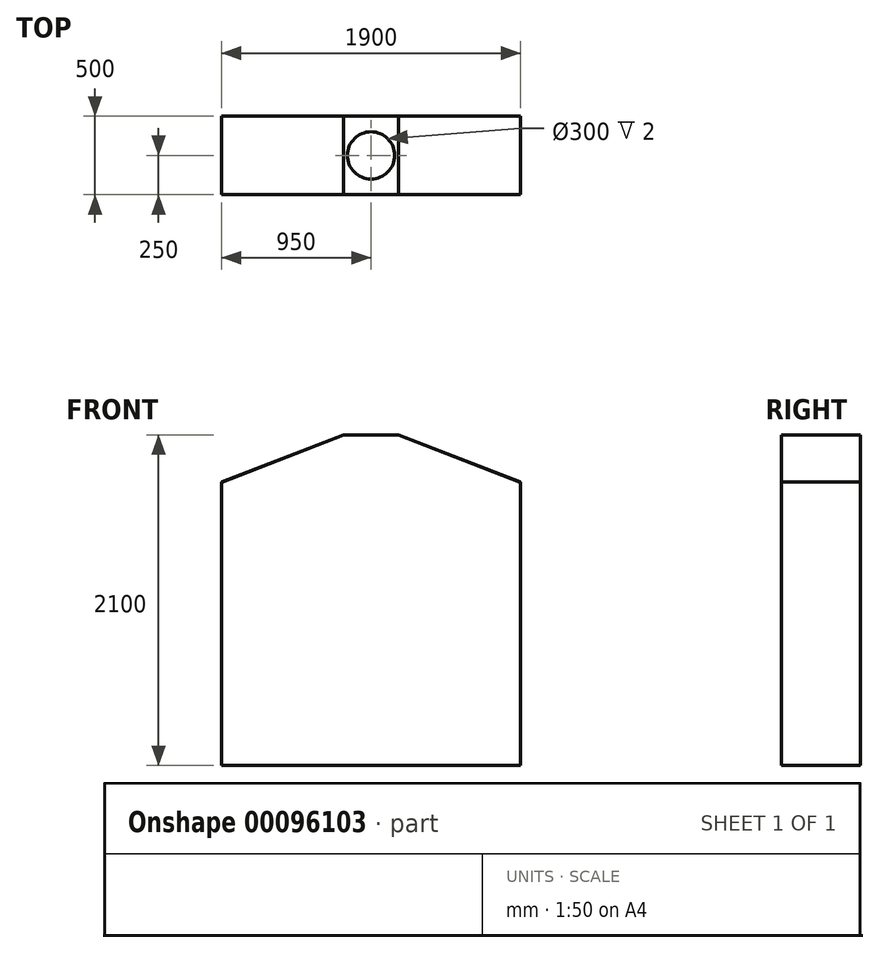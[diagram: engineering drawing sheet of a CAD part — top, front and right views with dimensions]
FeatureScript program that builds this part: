
annotation { "Feature Type Name" : "Feature", "Feature Type Description" : "" }
export const myFeature = defineFeature(function(context is Context, id is Id, definition is map)
    precondition{}
    {
        {
            var Q0;
            Q0=qCreatedBy(makeId("Front.planeOp"),FACE);
            var sketch = newSketch(context, id + "F0", { "sketchPlane" : qUnion([Q0])});
            skLineSegment(sketch, "E0.bottom", {"start": v(950, -900) * mm, "end": v(-950, -900) * mm});
            skLineSegment(sketch, "E0.top", {"start": v(950, 900) * mm, "end": v(-950, 900) * mm});
            skLineSegment(sketch, "E0.left", {"start": v(950, -900) * mm, "end": v(950, 900) * mm});
            skLineSegment(sketch, "E0.right", {"start": v(-950, -900) * mm, "end": v(-950, 900) * mm});
            skPoint(sketch, "E0.middle", {"position": v(0, 0) * mm});
            skLineSegment(sketch, "E1", {"start": v(0, 1200) * mm, "end": v(-175, 1200) * mm});
            skLineSegment(sketch, "E2", {"start": v(0, 1200) * mm, "end": v(175, 1200) * mm});
            skLineSegment(sketch, "E3", {"start": v(-950, 900) * mm, "end": v(-175, 1200) * mm});
            skLineSegment(sketch, "E4", {"start": v(175, 1200) * mm, "end": v(950, 900) * mm});
            skSolve(sketch);
        }
        {
            var Q0;
            Q0 = qSketchRegion(id + "F0", true);
            extrude(context, id + "F1", {"entities" : qUnion([Q0]), "endBound" : BoundingType.SYMMETRIC, "depth" : 500 * mm});
        }
        {
            var Q0;
            Q0=makeQuery(id+"F1.opExtrude","CAP_FACE",FACE,{"disambiguationData":[OSD([sQuery(id+"F0.wireOp",EDGE,"E0.bottom"),sQuery(id+"F0.wireOp",EDGE,"E0.left"),sQuery(id+"F0.wireOp",EDGE,"E0.right"),sQuery(id+"F0.wireOp",EDGE,"E1"),sQuery(id+"F0.wireOp",EDGE,"E2"),sQuery(id+"F0.wireOp",EDGE,"E3"),sQuery(id+"F0.wireOp",EDGE,"E4")])],"isStart":false});
            shell(context, id + "F2", {"entities" : qUnion([Q0]), "thickness" : 2 * mm});
        }
        {
            var Q0;
            Q0=qCreatedBy(makeId("Top.planeOp"),FACE);
            var sketch = newSketch(context, id + "F3", { "sketchPlane" : qUnion([Q0])});
            skCircle(sketch, "E5", {"center": v(0, 0) * mm, "radius": 150 * mm});
            skCircle(sketch, "E6", {"center": v(0, 0) * mm, "radius": 148 * mm});
            skSolve(sketch);
        }
        {
            var Q0;
            Q0=sQuery(id+"F3.wireOp",VERTEX,"E5.center");
            var Q1;
            Q1=makeQuery(id+"F1.opExtrude","SWEPT_BODY",BODY,{"disambiguationData":[OSD([sQuery(id+"F0.wireOp",EDGE,"E0.bottom"),sQuery(id+"F0.wireOp",EDGE,"E0.left"),sQuery(id+"F0.wireOp",EDGE,"E0.right"),sQuery(id+"F0.wireOp",EDGE,"E1"),sQuery(id+"F0.wireOp",EDGE,"E2"),sQuery(id+"F0.wireOp",EDGE,"E3"),sQuery(id+"F0.wireOp",EDGE,"E4")])]});
            hole(context, id + "F4", {"style" : HoleStyle.SIMPLE, "endStyle" : HoleEndStyle.THROUGH, "oppositeDirection" : true, "holeDiameter" : 300 * mm, "locations" : qUnion([Q0]), "scope" : qUnion([Q1]), "isTappedThrough" : true});
        }
    });
